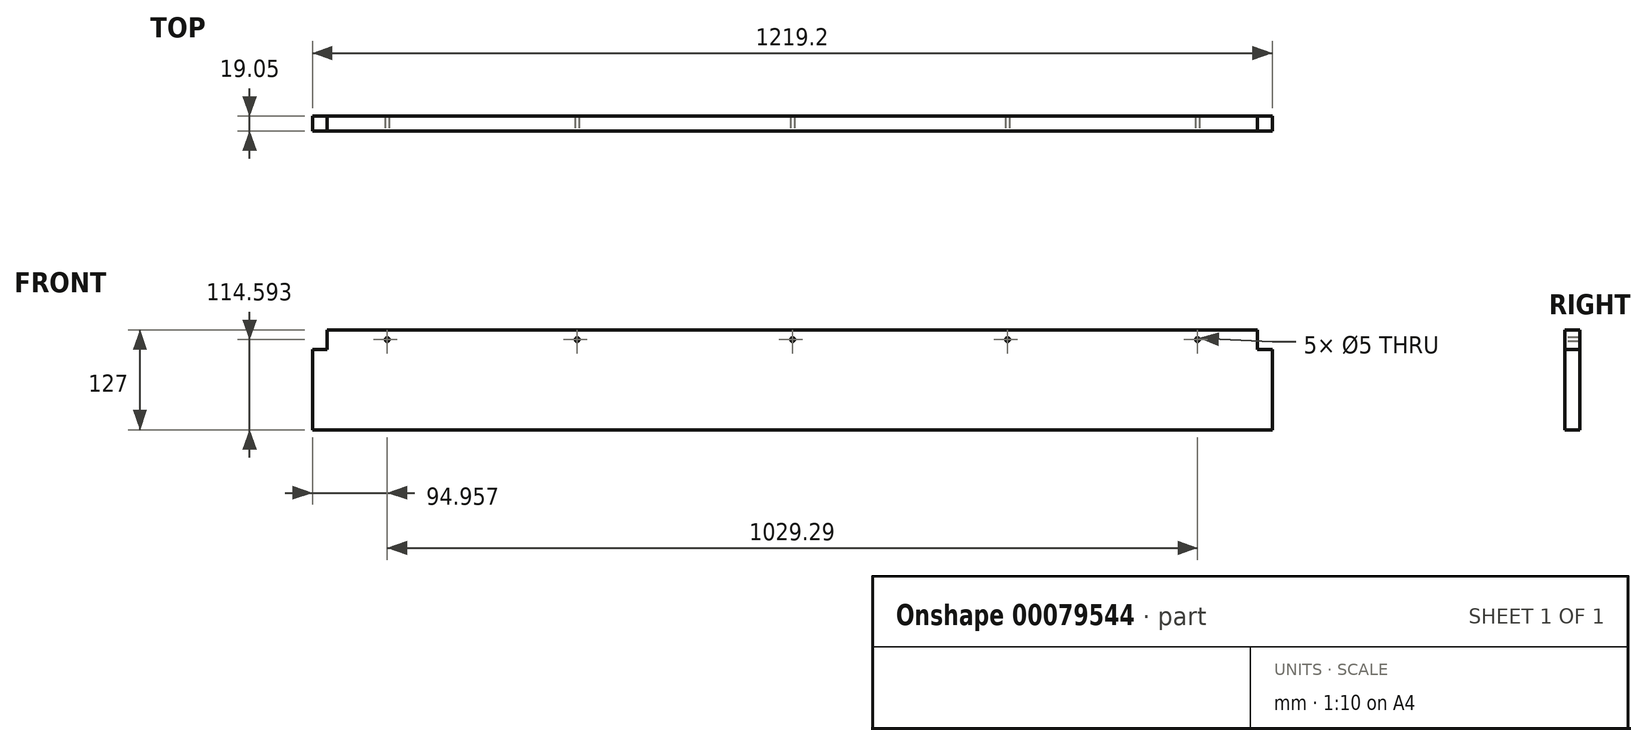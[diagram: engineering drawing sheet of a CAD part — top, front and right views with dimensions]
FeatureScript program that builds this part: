
annotation { "Feature Type Name" : "Feature", "Feature Type Description" : "" }
export const myFeature = defineFeature(function(context is Context, id is Id, definition is map)
    precondition{}
    {
        {
            var Q0;
            Q0=qCreatedBy(makeId("Front.planeOp"),FACE);
            var sketch = newSketch(context, id + "F0", { "sketchPlane" : qUnion([Q0])});
            skLineSegment(sketch, "E0.bottom", {"start": v(-609.6, -63.5) * mm, "end": v(609.6, -63.5) * mm});
            skLineSegment(sketch, "E0.top", {"start": v(-609.6, 63.5) * mm, "end": v(609.6, 63.5) * mm});
            skLineSegment(sketch, "E0.left", {"start": v(-609.6, -63.5) * mm, "end": v(-609.6, 63.5) * mm});
            skLineSegment(sketch, "E0.right", {"start": v(609.6, -63.5) * mm, "end": v(609.6, 63.5) * mm});
            skPoint(sketch, "E0.middle", {"position": v(0, 0) * mm});
            skSolve(sketch);
        }
        {
            var Q0;
            Q0=makeQuery(id+"F0.imprint","IMPRINT",FACE,{"disambiguationData":[TD([[makeQuery(id+"F0.imprint","IMPRINT",EDGE,{"derivedFrom":sQuery(id+"F0.wireOp",EDGE,"E0.bottom")}),1.0]])]});
            extrude(context, id + "F1", {"entities" : qUnion([Q0]), "depth" : 19.05 * mm});
        }
        {
            var Q0;
            Q0=makeQuery(id+"F1.opExtrude","CAP_FACE",FACE,{"disambiguationData":[OSD([sQuery(id+"F0.wireOp",EDGE,"E0.bottom"),sQuery(id+"F0.wireOp",EDGE,"E0.top"),sQuery(id+"F0.wireOp",EDGE,"E0.left"),sQuery(id+"F0.wireOp",EDGE,"E0.right")])],"isStart":false});
            var sketch = newSketch(context, id + "F2", { "sketchPlane" : qUnion([Q0])});
            skLineSegment(sketch, "E1.bottom", {"start": v(-609.6, 63.5) * mm, "end": v(-590.84, 63.5) * mm});
            skLineSegment(sketch, "E1.top", {"start": v(-609.6, 38.4) * mm, "end": v(-590.84, 38.4) * mm});
            skLineSegment(sketch, "E1.left", {"start": v(-609.6, 63.5) * mm, "end": v(-609.6, 38.4) * mm});
            skLineSegment(sketch, "E1.right", {"start": v(-590.84, 63.5) * mm, "end": v(-590.84, 38.4) * mm});
            skLineSegment(sketch, "E2", {"start": v(0, 63.5) * mm, "end": v(0, -63.5) * mm, "construction": true});
            skLineSegment(sketch, "E3.MirrorCS", {"start": v(609.6, 63.5) * mm, "end": v(609.6, 38.4) * mm});
            skLineSegment(sketch, "E4.MirrorCS", {"start": v(609.6, 63.5) * mm, "end": v(590.84, 63.5) * mm});
            skLineSegment(sketch, "E5.MirrorCS", {"start": v(609.6, 38.4) * mm, "end": v(590.84, 38.4) * mm});
            skLineSegment(sketch, "E6.MirrorCS", {"start": v(590.84, 63.5) * mm, "end": v(590.84, 38.4) * mm});
            skSolve(sketch);
        }
        {
            var Q0;
            Q0=makeQuery(id+"F2.imprint","IMPRINT",FACE,{"disambiguationData":[TD([[makeQuery(id+"F2.imprint","IMPRINT",EDGE,{"derivedFrom":sQuery(id+"F2.wireOp",EDGE,"E1.bottom")}),-1.0]])]});
            var Q1;
            Q1=makeQuery(id+"F2.imprint","IMPRINT",FACE,{"disambiguationData":[TD([[makeQuery(id+"F2.imprint","IMPRINT",EDGE,{"derivedFrom":sQuery(id+"F2.wireOp",EDGE,"E3.MirrorCS")}),1.0]])]});
            extrude(context, id + "F3", {"entities" : qUnion([Q0, Q1]), "operationType" : NewBodyOperationType.REMOVE, "endBound" : BoundingType.THROUGH_ALL, "oppositeDirection" : true, "depth" : 25.4 * mm});
        }
        {
            var Q0;
            Q0=makeQuery(id+"F1.opExtrude","CAP_FACE",FACE,{"disambiguationData":[OSD([sQuery(id+"F0.wireOp",EDGE,"E0.bottom"),sQuery(id+"F0.wireOp",EDGE,"E0.top"),sQuery(id+"F0.wireOp",EDGE,"E0.left"),sQuery(id+"F0.wireOp",EDGE,"E0.right")])],"isStart":false});
            var sketch = newSketch(context, id + "F4", { "sketchPlane" : qUnion([Q0])});
            skPoint(sketch, "E7", {"position": v(-514.64, 51.1) * mm});
            skPoint(sketch, "E8", {"position": v(-273.34, 51.1) * mm});
            skPoint(sketch, "E9", {"position": v(0.3, 51.1) * mm});
            skPoint(sketch, "E10", {"position": v(273.34, 51.1) * mm});
            skPoint(sketch, "E11", {"position": v(514.64, 51.1) * mm});
            skSolve(sketch);
        }
        {
            var Q0;
            Q0=sQuery(id+"F4.wireOp",VERTEX,"E7");
            var Q1;
            Q1=sQuery(id+"F4.wireOp",VERTEX,"E8");
            var Q2;
            Q2=sQuery(id+"F4.wireOp",VERTEX,"E9");
            var Q3;
            Q3=sQuery(id+"F4.wireOp",VERTEX,"E10");
            var Q4;
            Q4=sQuery(id+"F4.wireOp",VERTEX,"E11");
            var Q5;
            Q5=makeQuery(id+"F1.opExtrude","SWEPT_BODY",BODY,{"disambiguationData":[OSD([sQuery(id+"F0.wireOp",EDGE,"E0.bottom"),sQuery(id+"F0.wireOp",EDGE,"E0.top"),sQuery(id+"F0.wireOp",EDGE,"E0.left"),sQuery(id+"F0.wireOp",EDGE,"E0.right")])]});
            hole(context, id + "F5", {"style" : HoleStyle.SIMPLE, "endStyle" : HoleEndStyle.THROUGH, "holeDiameter" : 5 * mm, "locations" : qUnion([Q0, Q1, Q2, Q3, Q4]), "scope" : qUnion([Q5]), "isTappedThrough" : true});
        }
    });
